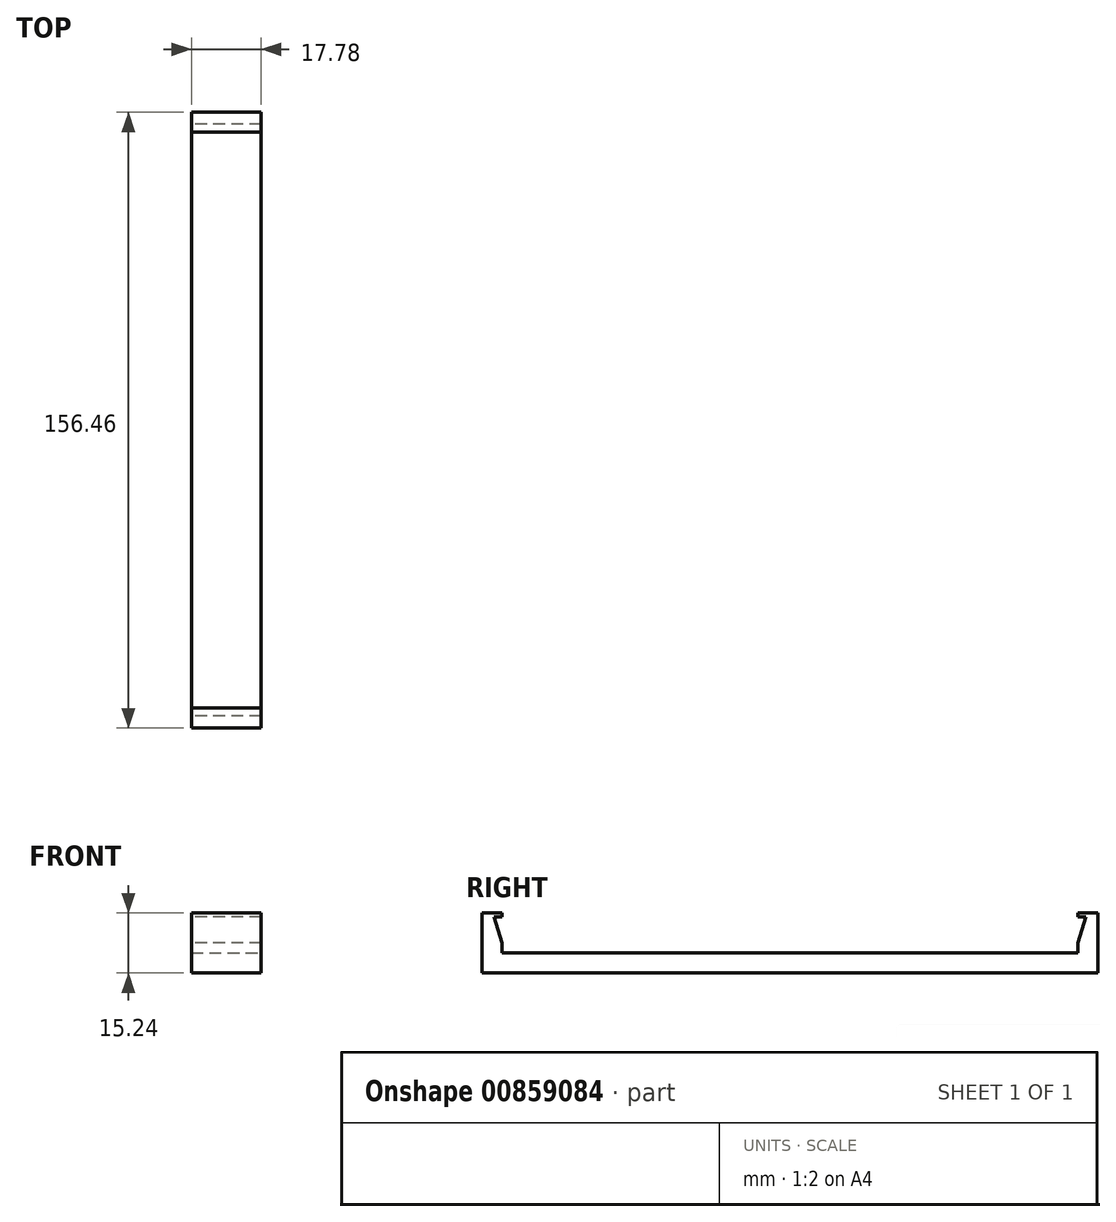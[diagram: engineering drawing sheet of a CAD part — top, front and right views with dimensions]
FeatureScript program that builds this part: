
annotation { "Feature Type Name" : "Feature", "Feature Type Description" : "" }
export const myFeature = defineFeature(function(context is Context, id is Id, definition is map)
    precondition{}
    {
        {
            var Q0;
            Q0=qCreatedBy(makeId("Top.planeOp"),FACE);
            var sketch = newSketch(context, id + "F0", { "sketchPlane" : qUnion([Q0])});
            skLineSegment(sketch, "E0.bottom", {"start": v(0, 0) * mm, "end": v(17.78, 0) * mm});
            skLineSegment(sketch, "E0.top", {"start": v(0, -156.46) * mm, "end": v(17.78, -156.46) * mm});
            skLineSegment(sketch, "E0.left", {"start": v(0, 0) * mm, "end": v(0, -156.46) * mm});
            skLineSegment(sketch, "E0.right", {"start": v(17.78, 0) * mm, "end": v(17.78, -156.46) * mm});
            skLineSegment(sketch, "E1", {"start": v(0, -78.23) * mm, "end": v(17.78, -78.23) * mm});
            skLineSegment(sketch, "E2", {"start": v(0, -151.38) * mm, "end": v(17.78, -151.38) * mm});
            skLineSegment(sketch, "E3", {"start": v(0, -5.08) * mm, "end": v(17.78, -5.08) * mm});
            skSolve(sketch);
        }
        {
            var Q0;
            {var subQ0=sQuery(id+"F0.wireOp",EDGE,"E1");Q0=makeQuery(id+"F0.imprint","IMPRINT",FACE,{"disambiguationData":[TD([[makeQuery(id+"F0.imprint","IMPRINT",EDGE,{"derivedFrom":subQ0}),1.0]])]});}
            var Q1;
            {var subQ0=sQuery(id+"F0.wireOp",EDGE,"E0.bottom");Q1=makeQuery(id+"F0.imprint","IMPRINT",FACE,{"disambiguationData":[TD([[makeQuery(id+"F0.imprint","IMPRINT",EDGE,{"derivedFrom":subQ0}),-1.0]])]});}
            var Q2;
            {var subQ0=sQuery(id+"F0.wireOp",EDGE,"E1");Q2=makeQuery(id+"F0.imprint","IMPRINT",FACE,{"disambiguationData":[TD([[makeQuery(id+"F0.imprint","IMPRINT",EDGE,{"derivedFrom":subQ0}),-1.0]])]});}
            var Q3;
            {var subQ0=sQuery(id+"F0.wireOp",EDGE,"E0.top");Q3=makeQuery(id+"F0.imprint","IMPRINT",FACE,{"disambiguationData":[TD([[makeQuery(id+"F0.imprint","IMPRINT",EDGE,{"derivedFrom":subQ0}),1.0]])]});}
            extrude(context, id + "F1", {"entities" : qUnion([Q0, Q1, Q2, Q3]), "oppositeDirection" : true, "depth" : 5.08 * mm, "offsetDistance" : 25.4 * mm});
        }
        {
            var Q0;
            {var subQ0=sQuery(id+"F0.wireOp",EDGE,"E0.bottom");Q0=makeQuery(id+"F0.imprint","IMPRINT",FACE,{"disambiguationData":[TD([[makeQuery(id+"F0.imprint","IMPRINT",EDGE,{"derivedFrom":subQ0}),-1.0]])]});}
            var Q1;
            {var subQ0=sQuery(id+"F0.wireOp",EDGE,"E0.top");Q1=makeQuery(id+"F0.imprint","IMPRINT",FACE,{"disambiguationData":[TD([[makeQuery(id+"F0.imprint","IMPRINT",EDGE,{"derivedFrom":subQ0}),1.0]])]});}
            extrude(context, id + "F2", {"entities" : qUnion([Q0, Q1]), "operationType" : NewBodyOperationType.ADD, "depth" : 10.16 * mm, "offsetDistance" : 25.4 * mm});
        }
        {
            var Q0;
            {var subQ0=sQuery(id+"F0.wireOp",EDGE,"E0.left");Q0=makeQuery(id+"F2.boolean.opBoolean","MERGE",FACE,{"derivedFrom":[makeQuery(id+"F1.opExtrude","SWEPT_FACE",FACE,{"disambiguationData":[OSD([subQ0])]}),makeQuery(id+"F2.opExtrude","SWEPT_FACE",FACE,{"disambiguationData":[OSD([subQ0]),TDD([makeQuery(id+"F0.imprint","IMPRINT",EDGE,{"disambiguationData":[TD([[makeQuery(id+"F0.imprint","INTERSECT",VERTEX,{"derivedFrom":[sQuery(id+"F0.wireOp",EDGE,"E0.bottom"),subQ0]}),-1.0]])],"derivedFrom":subQ0})])]}),makeQuery(id+"F2.opExtrude","SWEPT_FACE",FACE,{"disambiguationData":[OSD([subQ0]),TDD([makeQuery(id+"F0.imprint","IMPRINT",EDGE,{"disambiguationData":[TD([[makeQuery(id+"F0.imprint","INTERSECT",VERTEX,{"derivedFrom":[sQuery(id+"F0.wireOp",EDGE,"E0.top"),subQ0]}),1.0]])],"derivedFrom":subQ0})])]})]});}
            var sketch = newSketch(context, id + "F3", { "sketchPlane" : qUnion([Q0])});
            skLineSegment(sketch, "E4", {"start": v(5.08, 0) * mm, "end": v(5.08, 9.14) * mm});
            skLineSegment(sketch, "E5", {"start": v(78.23, 0) * mm, "end": v(78.23, -5.08) * mm});
            skLineSegment(sketch, "E6", {"start": v(5.08, 9.14) * mm, "end": v(3.05, 9.14) * mm});
            skLineSegment(sketch, "E7.MirrorCS", {"start": v(151.38, 9.14) * mm, "end": v(153.42, 9.14) * mm});
            skPoint(sketch, "E8", {"position": v(5.08, 2.54) * mm});
            skLineSegment(sketch, "E9", {"start": v(3.05, 9.14) * mm, "end": v(5.08, 2.54) * mm});
            skPoint(sketch, "E10.MirrorP", {"position": v(151.38, 2.54) * mm});
            skLineSegment(sketch, "E11.MirrorCS", {"start": v(151.38, 0) * mm, "end": v(151.38, 9.14) * mm});
            skLineSegment(sketch, "E12.MirrorCS", {"start": v(153.42, 9.14) * mm, "end": v(151.38, 2.54) * mm});
            skSolve(sketch);
        }
        {
            var Q0;
            Q0=makeQuery(id+"F3.imprint","IMPRINT",FACE,{"disambiguationData":[TD([[makeQuery(id+"F3.imprint","IMPRINT",EDGE,{"derivedFrom":sQuery(id+"F3.wireOp",EDGE,"E4")}),-1.0]])]});
            var Q1;
            Q1=makeQuery(id+"F3.imprint","IMPRINT",FACE,{"disambiguationData":[TD([[makeQuery(id+"F3.imprint","IMPRINT",EDGE,{"derivedFrom":sQuery(id+"F3.wireOp",EDGE,"9fda2d70-08d8-40b9-8583-a337d700c6220.MirrorCS")}),1.0]])]});
            var Q2;
            {var subQ0=sQuery(id+"F3.wireOp",EDGE,"E7.MirrorCS");Q2=makeQuery(id+"F3.imprint","IMPRINT",FACE,{"disambiguationData":[TD([[makeQuery(id+"F3.imprint","IMPRINT",EDGE,{"derivedFrom":subQ0}),-1.0]])]});}
            extrude(context, id + "F4", {"entities" : qUnion([Q0, Q1, Q2]), "operationType" : NewBodyOperationType.REMOVE, "oppositeDirection" : true, "depth" : 25.4 * mm, "offsetDistance" : 25.4 * mm});
        }
    });
